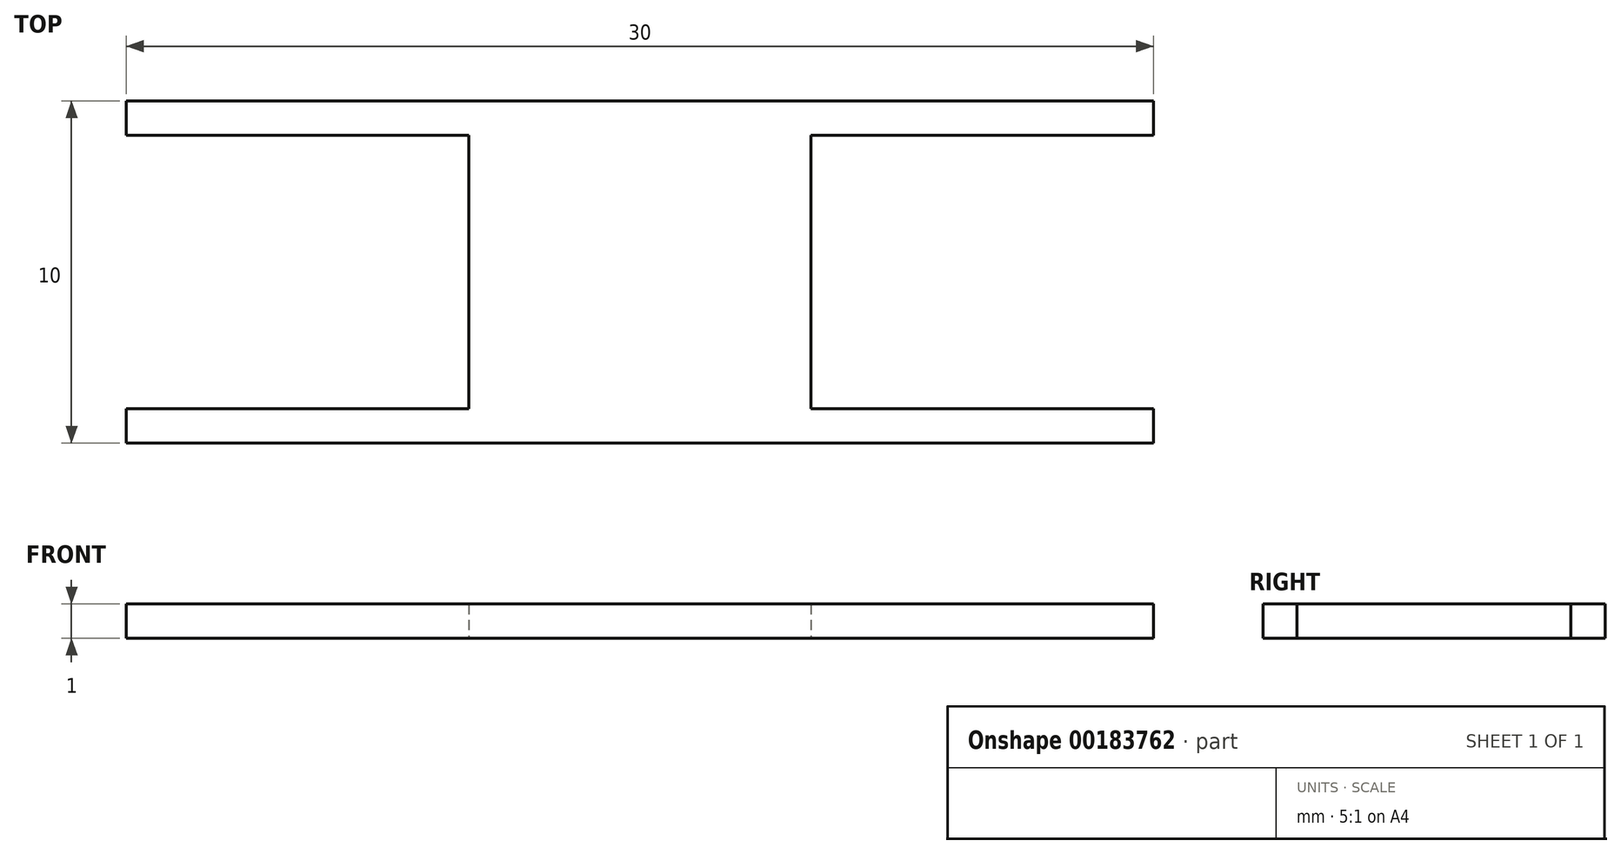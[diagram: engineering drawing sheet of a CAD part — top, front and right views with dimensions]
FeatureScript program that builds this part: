
annotation { "Feature Type Name" : "Feature", "Feature Type Description" : "" }
export const myFeature = defineFeature(function(context is Context, id is Id, definition is map)
    precondition{}
    {
        {
            var Q0;
            Q0=qCreatedBy(makeId("Top.planeOp"),FACE);
            var sketch = newSketch(context, id + "F0", { "sketchPlane" : qUnion([Q0])});
            skLineSegment(sketch, "E0.bottom", {"start": v(0, 0) * mm, "end": v(10, 0) * mm});
            skLineSegment(sketch, "E0.top", {"start": v(0, -10) * mm, "end": v(10, -10) * mm});
            skLineSegment(sketch, "E0.left", {"start": v(0, 0) * mm, "end": v(0, -10) * mm});
            skLineSegment(sketch, "E0.right", {"start": v(10, 0) * mm, "end": v(10, -10) * mm});
            skLineSegment(sketch, "E1.bottom", {"start": v(10, 0) * mm, "end": v(20, 0) * mm});
            skLineSegment(sketch, "E1.top", {"start": v(10, -1) * mm, "end": v(20, -1) * mm});
            skLineSegment(sketch, "E1.left", {"start": v(10, 0) * mm, "end": v(10, -1) * mm});
            skLineSegment(sketch, "E1.right", {"start": v(20, 0) * mm, "end": v(20, -1) * mm});
            skLineSegment(sketch, "E2.bottom", {"start": v(10, -10) * mm, "end": v(20, -10) * mm});
            skLineSegment(sketch, "E2.top", {"start": v(10, -9) * mm, "end": v(20, -9) * mm});
            skLineSegment(sketch, "E2.left", {"start": v(10, -10) * mm, "end": v(10, -9) * mm});
            skLineSegment(sketch, "E2.right", {"start": v(20, -10) * mm, "end": v(20, -9) * mm});
            skLineSegment(sketch, "E3.bottom", {"start": v(0, -10) * mm, "end": v(-10, -10) * mm});
            skLineSegment(sketch, "E3.top", {"start": v(0, -9) * mm, "end": v(-10, -9) * mm});
            skLineSegment(sketch, "E3.left", {"start": v(0, -10) * mm, "end": v(0, -9) * mm});
            skLineSegment(sketch, "E3.right", {"start": v(-10, -10) * mm, "end": v(-10, -9) * mm});
            skLineSegment(sketch, "E4.bottom", {"start": v(0, 0) * mm, "end": v(-10, 0) * mm});
            skLineSegment(sketch, "E4.top", {"start": v(0, -1) * mm, "end": v(-10, -1) * mm});
            skLineSegment(sketch, "E4.left", {"start": v(0, 0) * mm, "end": v(0, -1) * mm});
            skLineSegment(sketch, "E4.right", {"start": v(-10, 0) * mm, "end": v(-10, -1) * mm});
            skSolve(sketch);
        }
        {
            var Q0;
            Q0 = qSketchRegion(id + "F0", true);
            extrude(context, id + "F1", {"entities" : qUnion([Q0]), "depth" : 1 * mm});
        }
    });
